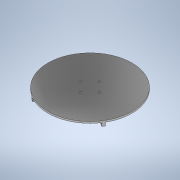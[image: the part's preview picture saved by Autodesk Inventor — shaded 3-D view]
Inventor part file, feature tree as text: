
AUTODESK INVENTOR PART (.ipt)
format: ipt  version: 2021 (Build 250183000, 183)  size: 164,864 bytes
history: native  units: mm
features: sketch x3, extrude x2, revolve x1, thread x1
ambient origin geometry x8: Origin, YZ Plane, XZ Plane, XY Plane, X Axis, Y Axis, Z Axis, Center Point
bodies: Solid1 (feature_tree)
feature tree (7):
  revolve  "Revolution1"  [1 undecoded]
  thread  "Thread1"  [1 undecoded]
  extrude  "Extrusion1"  Depth=3.0mm
  extrude  "Extrusion3"  Depth=6.0mm
  sketch  "Sketch1"  dims[d0=4.0mm d1=6.0mm d2=0.0mm]
  sketch  "Sketch2"  dims[d3=3.0mm d4=2.0mm]
  sketch  "Sketch5"  dims[d7=2.5mm d8=60.0mm d9=13.95mm d10=0.0mm d11=90.0deg d12=8.0mm d13=0.0mm d14=3.2mm d15=3.2mm d16=3.2mm d17=3.2mm d18=34.0mm d19=17.0mm d20=34.0mm d21=17.0mm d22=0.0mm d23=0.0mm d32=4.0mm d33=40.0mm d35=360.0deg d37=6.0mm d38=0.0mm]
note: 2 required parameter values undecoded (feature->parameter linkage not recoverable at this tier; creation-order binding heuristic only, values carry confidence <= 0.55)